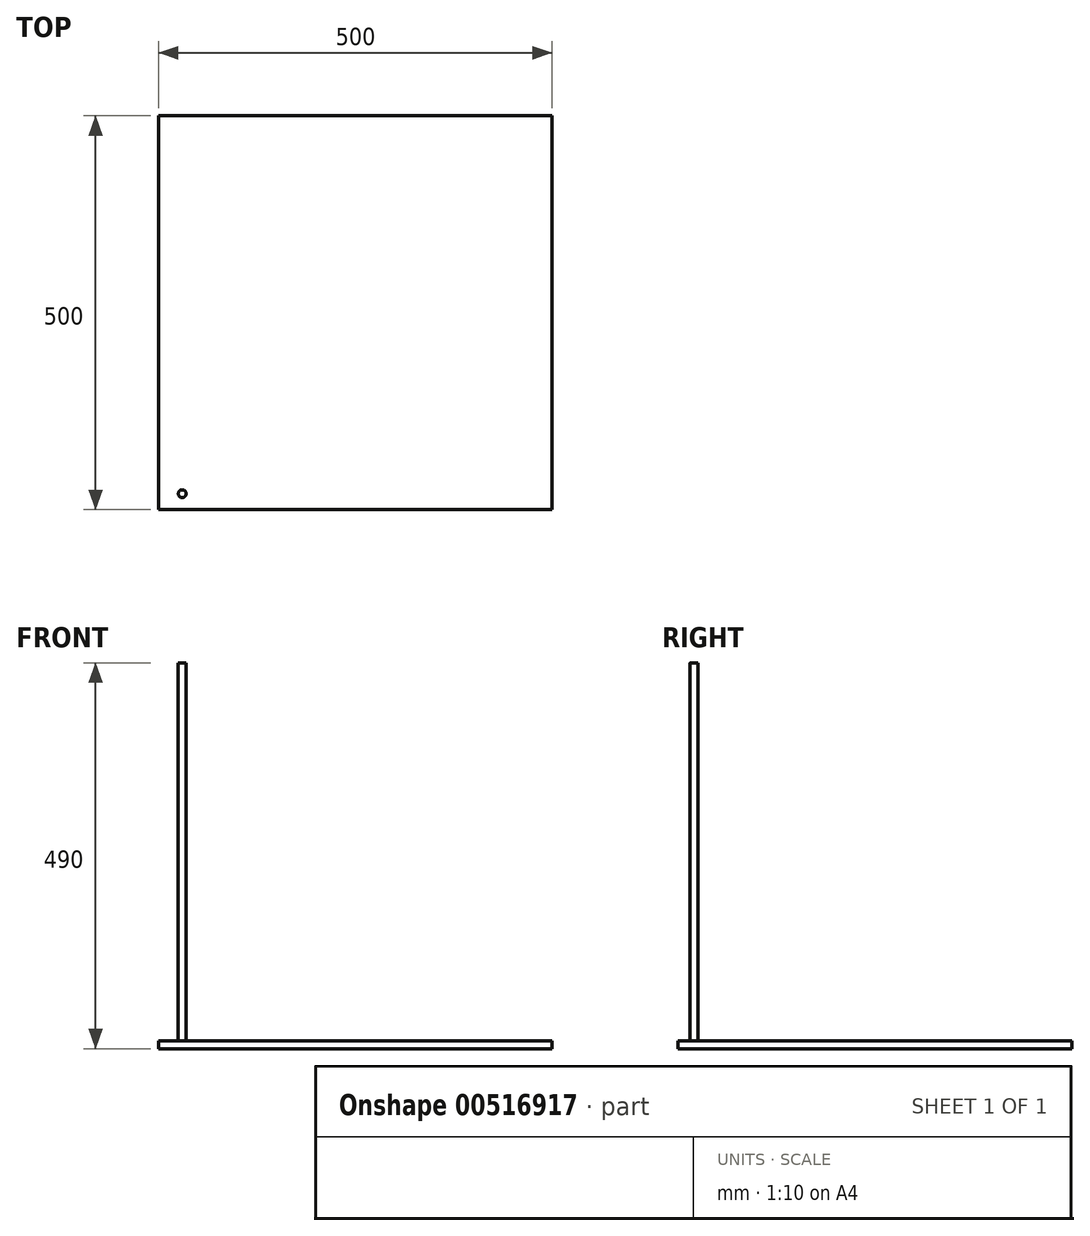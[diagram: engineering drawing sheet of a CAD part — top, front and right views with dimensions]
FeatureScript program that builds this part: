
annotation { "Feature Type Name" : "Feature", "Feature Type Description" : "" }
export const myFeature = defineFeature(function(context is Context, id is Id, definition is map)
    precondition{}
    {
        {
            var Q0;
            Q0=qCreatedBy(makeId("Top.planeOp"),FACE);
            var sketch = newSketch(context, id + "F0", { "sketchPlane" : qUnion([Q0])});
            skLineSegment(sketch, "E0.bottom", {"start": v(-250, 250) * mm, "end": v(250, 250) * mm});
            skLineSegment(sketch, "E0.top", {"start": v(-250, -250) * mm, "end": v(250, -250) * mm});
            skLineSegment(sketch, "E0.left", {"start": v(-250, 250) * mm, "end": v(-250, -250) * mm});
            skLineSegment(sketch, "E0.right", {"start": v(250, 250) * mm, "end": v(250, -250) * mm});
            skPoint(sketch, "E0.middle", {"position": v(0, 0) * mm});
            skSolve(sketch);
        }
        {
            var Q0;
            Q0 = qSketchRegion(id + "F0", true);
            extrude(context, id + "F1", {"entities" : qUnion([Q0]), "depth" : 10 * mm, "offsetDistance" : 25 * mm});
        }
        {
            var Q0;
            Q0=makeQuery(id+"F1.opExtrude","CAP_FACE",FACE,{"disambiguationData":[OSD([sQuery(id+"F0.wireOp",EDGE,"E0.bottom"),sQuery(id+"F0.wireOp",EDGE,"E0.top"),sQuery(id+"F0.wireOp",EDGE,"E0.left"),sQuery(id+"F0.wireOp",EDGE,"E0.right")])],"isStart":false});
            var sketch = newSketch(context, id + "F2", { "sketchPlane" : qUnion([Q0])});
            skCircle(sketch, "E1", {"center": v(-220, -230) * mm, "radius": 5 * mm});
            skSolve(sketch);
        }
        {
            var Q0;
            Q0 = qSketchRegion(id + "F2", true);
            extrude(context, id + "F3", {"entities" : qUnion([Q0]), "depth" : 480 * mm, "offsetDistance" : 25 * mm});
        }
    });
